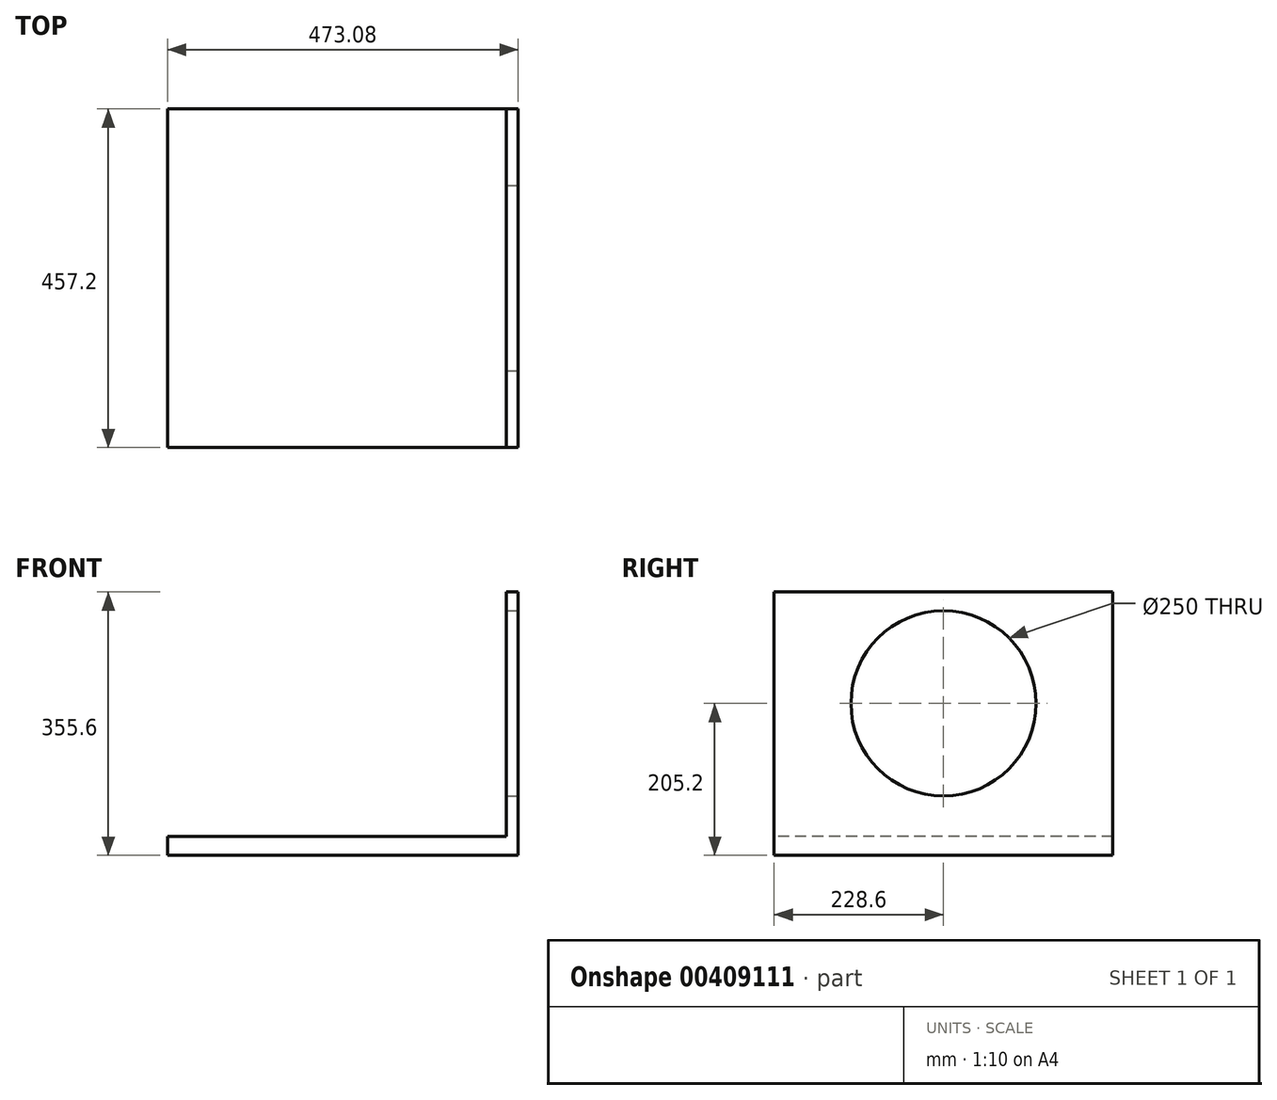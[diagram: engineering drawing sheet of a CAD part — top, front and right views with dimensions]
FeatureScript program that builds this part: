
annotation { "Feature Type Name" : "Feature", "Feature Type Description" : "" }
export const myFeature = defineFeature(function(context is Context, id is Id, definition is map)
    precondition{}
    {
        {
            var Q0;
            Q0=qCreatedBy(makeId("Top.planeOp"),FACE);
            var sketch = newSketch(context, id + "F0", { "sketchPlane" : qUnion([Q0])});
            skLineSegment(sketch, "E0.bottom", {"start": v(228.6, 228.6) * mm, "end": v(-228.6, 228.6) * mm});
            skLineSegment(sketch, "E0.top", {"start": v(228.6, -228.6) * mm, "end": v(-228.6, -228.6) * mm});
            skLineSegment(sketch, "E0.left", {"start": v(228.6, 228.6) * mm, "end": v(228.6, -228.6) * mm});
            skLineSegment(sketch, "E0.right", {"start": v(-228.6, 228.6) * mm, "end": v(-228.6, -228.6) * mm});
            skPoint(sketch, "E0.middle", {"position": v(0, 0) * mm});
            skSolve(sketch);
        }
        {
            var Q0;
            Q0 = qSketchRegion(id + "F0", true);
            extrude(context, id + "F1", {"entities" : qUnion([Q0]), "depth" : 25.4 * mm});
        }
        {
            var Q0;
            Q0=makeQuery(id+"F1.opExtrude","SWEPT_FACE",FACE,{"disambiguationData":[OSD([sQuery(id+"F0.wireOp",EDGE,"E0.left")])]});
            var sketch = newSketch(context, id + "F2", { "sketchPlane" : qUnion([Q0])});
            skLineSegment(sketch, "E1.bottom", {"start": v(-228.6, 0) * mm, "end": v(228.6, 0) * mm});
            skLineSegment(sketch, "E1.top", {"start": v(-228.6, 355.6) * mm, "end": v(228.6, 355.6) * mm});
            skLineSegment(sketch, "E1.left", {"start": v(-228.6, 0) * mm, "end": v(-228.6, 355.6) * mm});
            skLineSegment(sketch, "E1.right", {"start": v(228.6, 0) * mm, "end": v(228.6, 355.6) * mm});
            skSolve(sketch);
        }
        {
            var Q0;
            Q0 = qSketchRegion(id + "F2", true);
            extrude(context, id + "F3", {"entities" : qUnion([Q0]), "operationType" : NewBodyOperationType.ADD, "depth" : 15.88 * mm});
        }
        {
            var Q0;
            Q0=makeQuery(id+"F3.opExtrude","CAP_FACE",FACE,{"disambiguationData":[OSD([sQuery(id+"F2.wireOp",EDGE,"E1.bottom"),sQuery(id+"F2.wireOp",EDGE,"E1.top"),sQuery(id+"F2.wireOp",EDGE,"E1.left"),sQuery(id+"F2.wireOp",EDGE,"E1.right")])],"isStart":false});
            var sketch = newSketch(context, id + "F4", { "sketchPlane" : qUnion([Q0])});
            skCircle(sketch, "E2", {"center": v(0, 205.2) * mm, "radius": 125 * mm});
            skSolve(sketch);
        }
        {
            var Q0;
            Q0 = qSketchRegion(id + "F4", true);
            extrude(context, id + "F5", {"entities" : qUnion([Q0]), "operationType" : NewBodyOperationType.REMOVE, "endBound" : BoundingType.UP_TO_NEXT, "oppositeDirection" : true, "depth" : 25.4 * mm});
        }
    });
